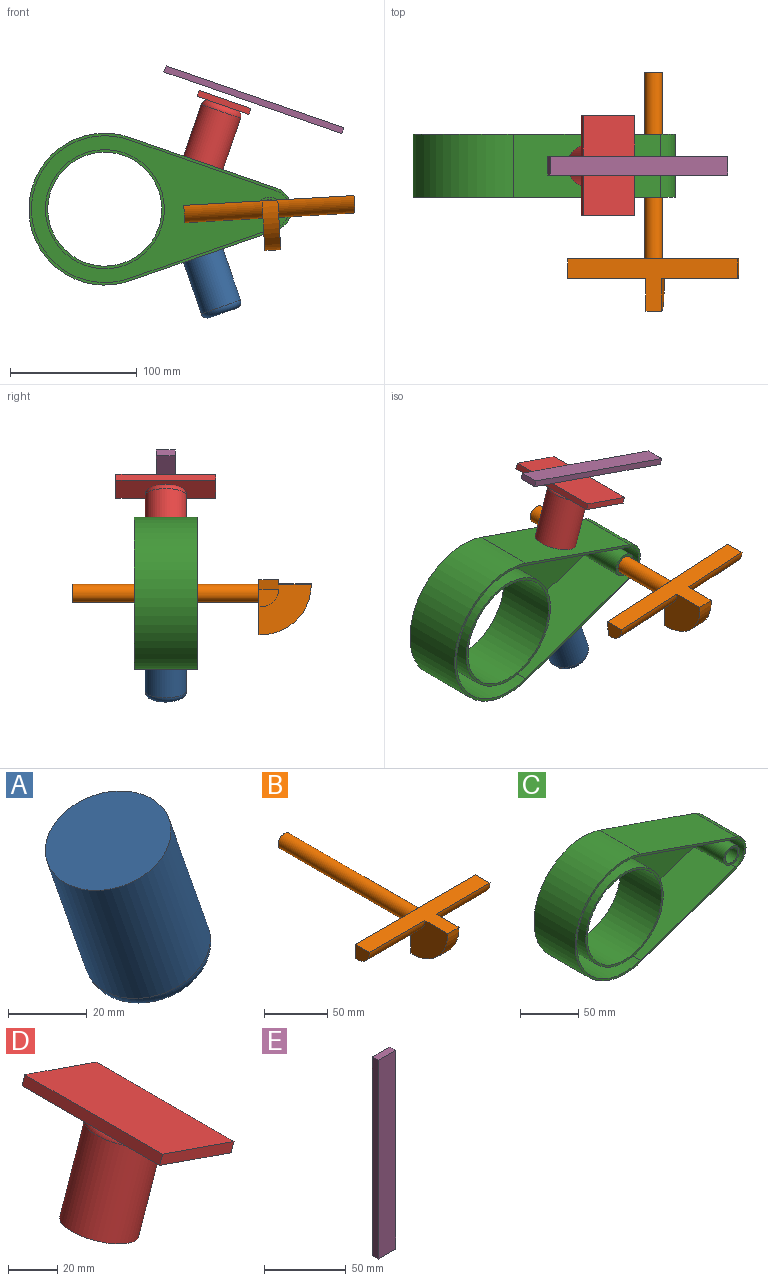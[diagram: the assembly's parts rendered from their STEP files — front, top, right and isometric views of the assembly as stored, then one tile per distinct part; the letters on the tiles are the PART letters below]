
ASSEMBLY  parts=5 mates=4
PART A: 4 faces, bbox 46.4x35.5x54.8 mm
  f0: cylinder r=16.41mm len=51.37mm, axis (-0.33,0,0.95), area 4433.7mm2, adj f2,f3
  f1: plane 22.82x21.57mm, normal (0.33,0,-0.95), area 409mm2, adj f3
  f2: plane 32.82x31.02mm, normal (-0.33,0,0.95), area 846mm2, adj f0
  f3: torus R=11.41mm, axis (0.33,0,-0.95), area 720.2mm2, adj f0,f1
PART B: 15 faces, bbox 134.6x188.4x39.5 mm
  f0: cylinder r=7mm len=147mm, axis (0,1,0), area 6465.4mm2, adj f1,f2,f3
  f1: plane 2.57x0.12mm, normal (0,-1,0), area 0.2mm2, adj f0,f4
  f2: plane 14x14mm, normal (0,1,0), area 153.9mm2, adj f0
  f3: plane 134.65x39.39mm, normal (0,1,0), area 2021.5mm2, adj f0,f4,f5,f6,f7,f8,f9,f10
  f4: plane 134.65x41.39mm, normal (0,0,1), area 2444.5mm2, adj f1,f3,f5,f7,f9,f11,f12,f13
  f5: plane 15.76x13.76mm, normal (-1,0,0), area 176.3mm2, adj f3,f4,f6,f12
  f6: plane 61.85x2mm, normal (0,0,-1), area 123.7mm2, adj f3,f5,f7,f12
  f7: plane 41.39x39.39mm, normal (-1,0,0), area 1120.9mm2, adj f3,f4,f6,f8,f12,f13
  f8: plane 12.57x2mm, normal (0,0,-1), area 25.1mm2, adj f3,f7,f9,f13
  f9: plane 41.39x39.39mm, normal (1,0,0), area 1120.9mm2, adj f3,f4,f8,f10,f13,f14
  f10: plane 60.23x2mm, normal (0,0,-1), area 120.5mm2, adj f3,f9,f11,f14
  f11: plane 15.76x13.76mm, normal (1,0,0), area 176.3mm2, adj f3,f4,f10,f14
  f12: cylinder r=13.76mm len=61.85mm, axis (1,0,0), area 1337mm2, adj f4,f5,f6,f7
  f13: cylinder r=39.39mm len=39.39mm, axis (1,0,0), area 777.8mm2, adj f4,f7,f8,f9
  f14: cylinder r=13.76mm len=60.23mm, axis (1,0,0), area 1302.1mm2, adj f4,f9,f10,f11
PART C: 17 faces, bbox 207.5x50x120 mm
  f0: plane 19x19mm, normal (0,-1,0), area 106.8mm2, adj f9,f16
  f1: plane 94x94mm, normal (0,-1,0), area 578.1mm2, adj f6,f14
  f2: cylinder r=17.5mm len=50mm, axis (0,1,0), area 2166.1mm2, adj f3,f5,f7,f8
  f3: plane 116.11x50mm, normal (0.33,0,0.95), area 6142.8mm2, adj f2,f4,f7,f8
  f4: cylinder r=60mm len=120mm, axis (0,1,0), area 11423.1mm2, adj f3,f5,f7,f8
  f5: plane 116.11x50mm, normal (0.33,0,-0.95), area 6142.8mm2, adj f2,f4,f7,f8
  f6: cylinder r=45mm len=90mm, axis (0,1,0), area 14137.2mm2, adj f1,f8
  f7: plane 207.5x120mm, normal (0,-1,0), area 1022.4mm2, adj f2,f3,f4,f5,f10,f11,f12,f13
  f8: plane 207.5x120mm, normal (0,1,0), area 10215.8mm2, adj f2,f3,f4,f5,f6,f9
  f9: cylinder r=7.5mm len=50mm, axis (0,-1,0), area 2356.2mm2, adj f0,f8
  f10: cylinder r=15.5mm len=48mm, axis (0,1,0), area 1841.8mm2, adj f7,f11,f13,f15
  f11: plane 116.11x48mm, normal (-0.33,0,-0.95), area 5897.1mm2, adj f7,f10,f12,f15
  f12: cylinder r=58mm len=116mm, axis (0,1,0), area 10600.6mm2, adj f7,f11,f13,f15
  f13: plane 116.11x48mm, normal (-0.33,0,0.95), area 5897.1mm2, adj f7,f10,f12,f15
  f14: cylinder r=47mm len=94mm, axis (0,1,0), area 14174.9mm2, adj f1,f15
  f15: plane 203.5x116mm, normal (0,-1,0), area 8508.5mm2, adj f10,f11,f12,f13,f14,f16
  f16: cylinder r=9.5mm len=48mm, axis (0,-1,0), area 2865.1mm2, adj f0,f15
PART D: 9 faces, bbox 53.3x78.8x62.5 mm
  f0: cylinder r=16.41mm len=51.37mm, axis (-0.33,0,-0.95), area 4433.7mm2, adj f1,f2
  f1: plane 32.82x31.02mm, normal (-0.33,0,-0.95), area 846mm2, adj f0
  f2: torus R=11.41mm, axis (0.33,0,0.95), area 720.2mm2, adj f0,f8
  f3: plane 42.5x18.86mm, normal (0,-1,0), area 216.2mm2, adj f4,f6,f7,f8
  f4: plane 78.77x4.73mm, normal (0.95,0,-0.33), area 393.8mm2, adj f3,f5,f7,f8
  f5: plane 42.5x18.86mm, normal (0,1,0), area 216.2mm2, adj f4,f6,f7,f8
  f6: plane 78.77x4.73mm, normal (-0.95,0,0.33), area 393.8mm2, adj f3,f5,f7,f8
  f7: plane 78.77x40.87mm, normal (0.33,0,0.95), area 3406mm2, adj f3,f4,f5,f6
  f8: plane 78.77x40.87mm, normal (-0.33,0,-0.95), area 2997mm2, adj f2,f3,f4,f5,f6
PART E: 6 faces, bbox 14.9x5x148.7 mm
  f0: plane 14.91x5mm, normal (0,0,1), area 74.5mm2, adj f1,f3,f4,f5
  f1: plane 148.7x5mm, normal (-1,0,0), area 743.5mm2, adj f0,f2,f4,f5
  f2: plane 14.91x5mm, normal (0,0,-1), area 74.5mm2, adj f1,f3,f4,f5
  f3: plane 148.7x5mm, normal (1,0,0), area 743.5mm2, adj f0,f2,f4,f5
  f4: plane 148.7x14.91mm, normal (0,-1,0), area 2216.5mm2, adj f0,f1,f2,f3
  f5: plane 148.7x14.91mm, normal (0,1,0), area 2216.5mm2, adj f0,f1,f2,f3
PLACE A rot(axis=(0.25,-0.43,-0.87),0deg) t=(19.81,38.84,30.97)mm
PLACE B rot(axis=(0,-1,0),3.3deg) t=(156.85,38.84,33.4)mm
PLACE C rot(axis=(0.25,-0.43,-0.87),0deg) t=(26.85,38.84,33.4)mm fixed
PLACE D rot(axis=(0.25,-0.43,-0.87),0deg) t=(65.81,38.84,21.04)mm
PLACE E rot(axis=(0.63,0.63,0.45),131.6deg) t=(143.76,38.84,122.81)mm
MATE slider E.f5 <-> D.f7  axis (0.33,0,0.95) through (145.46,38.84,122.22)mm
MATE revolute B.f0 <-> C.f2  axis (0,1,0) through (156.85,38.84,33.4)mm
MATE fastened D.f0 <-> C.f3  axis (-0.33,0,-0.95) through (104.52,38.84,70.02)mm
MATE fastened A.f0 <-> C.f5  axis (-0.33,0,0.95) through (104.52,38.84,-3.22)mm
